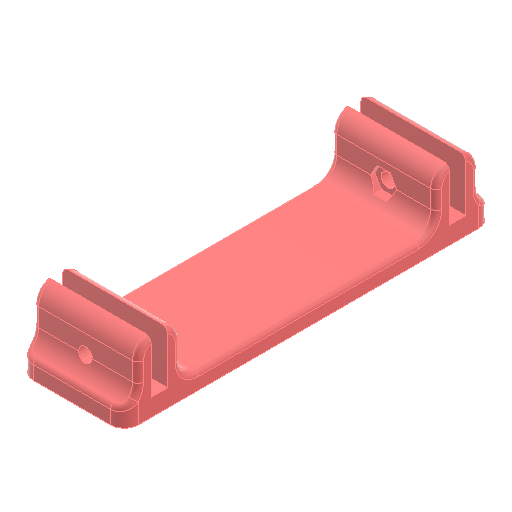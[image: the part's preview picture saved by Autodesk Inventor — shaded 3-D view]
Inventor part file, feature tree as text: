
AUTODESK INVENTOR PART (.ipt)
format: ipt  version: 2025 (Build 290162000, 162)  size: 316,416 bytes
history: native  units: mm
features: sketch x4, extrude x4, fillet x4, hole x1, plane x1, mirror x1, projected_geometry x1
ambient origin geometry x8: Origin, YZ Plane, XZ Plane, XY Plane, X Axis, Y Axis, Z Axis, Center Point
bodies: Solid1 (feature_tree)
feature tree (16):
  sketch  "Sketch1"  dims[d0=25.4mm d1=38.1mm]
  extrude  "Extrusion1"  Depth=38.1mm
  extrude  "Extrusion2"  Depth=6.35mm TaperAngle=0.0deg
  hole  "Hole1"  [1 undecoded]
  plane  "Work Plane1"
  extrude  "Extrusion4"  [1 undecoded]
  mirror  "Mirror1"
  extrude  "Extrusion3"  Depth=2.0mm TaperAngle=0.0deg
  fillet  "Fillet3"  Radius=6.35mm
  fillet  "Fillet4"  Radius=6.35mm
  fillet  "Fillet5"  Radius=8.25mm
  fillet  "Fillet6"  Radius=1.5mm
  sketch  "Sketch2"  dims[d2=6.0mm d5=6.35mm d6=0.0mm]
  projected_geometry  "Projected Loop1"
  sketch  "Sketch3"  dims[d7=25.4mm d8=0.0mm]
  sketch  "Sketch4"  dims[d9=5.0mm d10=6.0mm d11=4.0mm d12=2.0mm d13=90.0deg d14=8.0mm d15=20.594885mm d18=4.7625mm d20=-54.15mm d21=6.35mm d22=0.0mm d23=6.35mm d24=6.35mm d25=8.25mm d26=1.5mm d27=0.0mm d28=5.0mm d29=2.0mm d30=12.7mm]
note: 2 required parameter values undecoded (feature->parameter linkage not recoverable at this tier; creation-order binding heuristic only, values carry confidence <= 0.55)
